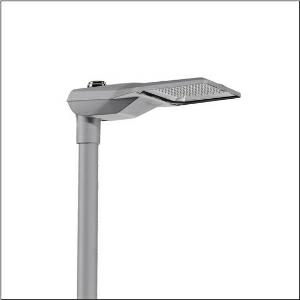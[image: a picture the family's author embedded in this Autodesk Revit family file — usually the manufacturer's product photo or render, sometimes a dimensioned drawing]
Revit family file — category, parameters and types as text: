
# Revit family: streetlight_sl_21_midi___st1_5a_5xe7p47n08lb_54ff
name_source: partatom
category: Lighting Fixtures
units: mm (PartAtom-declared; Revit-internal decimal feet)

## family parameters
Cut with Voids When Loaded = No
Host = Face
Light Source = No
Part Type = Normal
Room Calculation Point = No
Round Connector Dimension = Use Diameter
Shared = No

## types (1)
- --- (1 x LED, 14690 lm, 98.3 W, 4000K)
    Apparent Load = 98 VA
    CIE Flux Codes = 22 53 95 100 100
    Color Rendering = 70
    Color Temperature = 4000K
    Default Elevation = 1800 mm
    Description = Streetlight SL 21 midi, mast luminaire, primary light control with lens, of PMMA, primary optical cover: cover, of toughened safety glass, transparent, light distribution: ST1.5a, light emission: direct distribution, primary light characteristic: asymmetric, installation type: side-entry, LED, 3G 2.5mm², High Power LED, rated luminous flux: 14.690lm, luminous efficacy: 149lm/W, light colour: 740, colour temperature: 4000K, control gear: NEMA (7pin), control: overheat protection, pre-setting: linear dimming characteristic, constant luminous flux control, time-dependent luminous flux control, flexible luminous flux parameterisation, mains connection: 220..240V, AC, 50/60Hz, connection cable pre-assembled, cable length: 10,5m, wiring characteristics: H05VV-F, start of lifetime: 98W, end of service life: 101W, reduction: 45W, luminaire housing, of diecast aluminium (EN AC-44300), powder-coated, Siteco® metallic grey (DB 702S), corrosivity category C5 mid according to DIN EN ISO 12944, multi-level sealing system, sealing non-destructively replaceable, inclination adjustable: 0°, 5°, 10°, 15°, length: 644mm, width: 335mm, height: 110mm, spigot size: 42mm (side-entry), mounting height: 4..8m, protection rating (complete): IP66, insulation class (complete): insulation class I (protective earthing), certification: CE, ENEC, ENEC+, VDE, impact resistance: IK10, permissible operating ambient temperature for outdoor applications: -40..+50°C, standard-compliant lighting for roads and squares, packaging unit: 1 piece

Light Distribution: ST1.5a
    Height = 111 mm
    Lamp = 1 x LED
    Lamp Light Flux = 14690 lm
    Lamp Power = 98.3 W
    Lamp count = 1
    Length = 644 mm
    Luminous efficacy = 149 lm/W
    Manufacturer = Siteco
    ModVariant = No
    Model = 5XE7P47N08LB
    Number of Poles = 1
    OnlyDefault = Yes
    Power Factor = 1
    Product Name = Streetlight SL 21 midi | ST1.5a
    Product group = mast luminaire | pylon top
    ProductGroupID = 6100
    Protection Class = Protection class I
    Protection Degree = IP 66
    RLX_Detail_Level = 1
    RLX_Emergency_Light_Flux = 0 lm
    RLX_Emergency_Type = 0
    RLX_Emergency_Type_DB = No
    RlxData = <blob elided: 30281 chars, md5=af44b1f6>
    Socket = socket
    Standby Power = 0 W
    System Light Flux = 14690 lm
    System Power = 98 W
    Type Comments = factory setting: luminous flux: 100 % | dim-lin: 254 | 1020 mA
    Type Image = l_1294377.jpg
    URL = http://relux.com
    VarID = @adj_154901
    Voltage = 0 V
    Weight = 0.00 kg
    Width = 336 mm

## geometry (parser evidence)
native form markers: Blend x4, Sweep x10
no freeform markers — native parametric forms only
